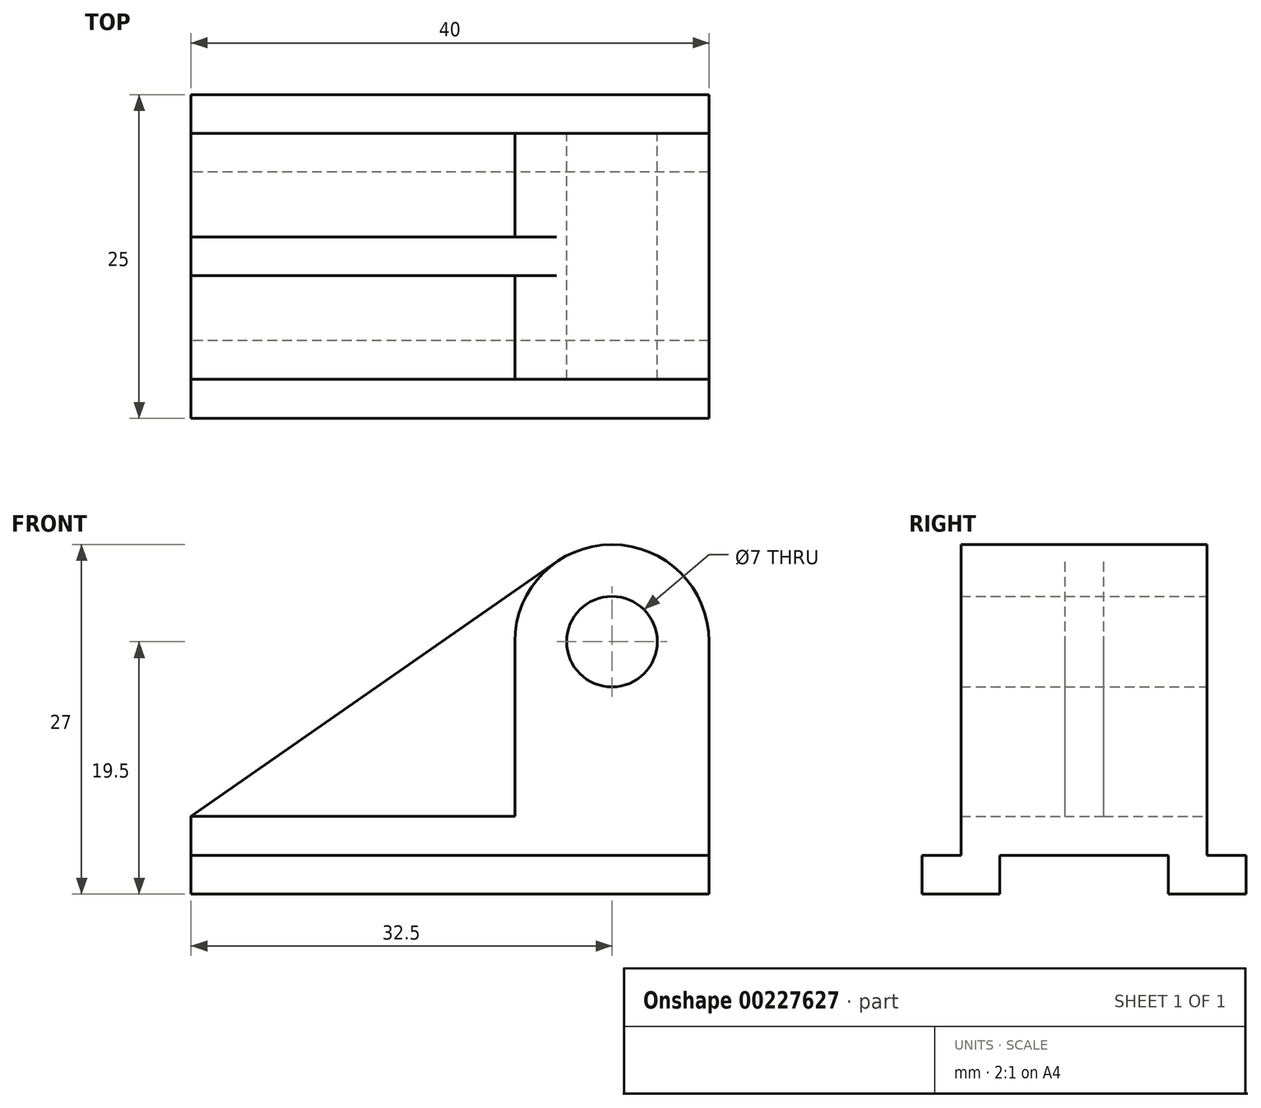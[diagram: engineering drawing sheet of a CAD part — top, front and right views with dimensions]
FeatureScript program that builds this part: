
annotation { "Feature Type Name" : "Feature", "Feature Type Description" : "" }
export const myFeature = defineFeature(function(context is Context, id is Id, definition is map)
    precondition{}
    {
        {
            var Q0;
            Q0=qCreatedBy(makeId("Right.planeOp"),FACE);
            var sketch = newSketch(context, id + "F0", { "sketchPlane" : qUnion([Q0])});
            skLineSegment(sketch, "E0", {"start": v(0, 0) * mm, "end": v(-6.5, 0) * mm});
            skLineSegment(sketch, "E1", {"start": v(-6.5, 0) * mm, "end": v(-6.5, -3) * mm});
            skLineSegment(sketch, "E2", {"start": v(-6.5, -3) * mm, "end": v(-12.5, -3) * mm});
            skLineSegment(sketch, "E3", {"start": v(-12.5, -3) * mm, "end": v(-12.5, 0) * mm});
            skLineSegment(sketch, "E4", {"start": v(-12.5, 0) * mm, "end": v(-9.5, 0) * mm});
            skLineSegment(sketch, "E5", {"start": v(-9.5, 0) * mm, "end": v(-9.5, 3) * mm});
            skLineSegment(sketch, "E6", {"start": v(-9.5, 3) * mm, "end": v(0, 3) * mm});
            skLineSegment(sketch, "E7", {"start": v(0, 3) * mm, "end": v(0, 0) * mm});
            skSolve(sketch);
        }
        {
            var Q0;
            Q0=makeQuery(id+"F0.imprint","IMPRINT",FACE,{"disambiguationData":[TD([[makeQuery(id+"F0.imprint","IMPRINT",EDGE,{"derivedFrom":sQuery(id+"F0.wireOp",EDGE,"E0")}),-1.0]])]});
            extrude(context, id + "F1", {"entities" : qUnion([Q0]), "depth" : 40 * mm});
        }
        {
            var Q0;
            Q0=makeQuery(id+"F1.opExtrude","SWEPT_BODY",BODY,{"disambiguationData":[OSD([sQuery(id+"F0.wireOp",EDGE,"E0"),sQuery(id+"F0.wireOp",EDGE,"E1"),sQuery(id+"F0.wireOp",EDGE,"E2"),sQuery(id+"F0.wireOp",EDGE,"E3"),sQuery(id+"F0.wireOp",EDGE,"E4"),sQuery(id+"F0.wireOp",EDGE,"E5"),sQuery(id+"F0.wireOp",EDGE,"E6"),sQuery(id+"F0.wireOp",EDGE,"E7")])]});
            var Q1;
            Q1=qCreatedBy(makeId("Front.planeOp"),FACE);
            mirror(context, id + "F2", {"operationType" : NewBodyOperationType.ADD, "entities" : qUnion([Q0]), "mirrorPlane" : qUnion([Q1])});
        }
        {
            var Q0;
            Q0=qCreatedBy(makeId("Front.planeOp"),FACE);
            var sketch = newSketch(context, id + "F3", { "sketchPlane" : qUnion([Q0])});
            skLineSegment(sketch, "E8.0", {"start": v(40, 3) * mm, "end": v(0, 3) * mm});
            skLineSegment(sketch, "E9", {"start": v(40, 3) * mm, "end": v(40, 16.5) * mm});
            skLineSegment(sketch, "E10", {"start": v(40, 16.5) * mm, "end": v(25, 16.5) * mm, "construction": true});
            skLineSegment(sketch, "E11", {"start": v(25, 16.5) * mm, "end": v(25, 3) * mm});
            skArc(sketch, "E12", {"start": v(40, 16.5) * mm, "mid": v(32.5, 24) * mm, "end": v(25, 16.5) * mm});
            skCircle(sketch, "E13", {"center": v(32.5, 16.5) * mm, "radius": 3.5 * mm});
            skLineSegment(sketch, "E14", {"start": v(28.62, 22.94) * mm, "end": v(0, 3) * mm});
            skSolve(sketch);
        }
        {
            var Q0;
            {var subQ1=sQuery(id+"F3.wireOp",EDGE,"E9");Q0=makeQuery(id+"F3.imprint","IMPRINT",FACE,{"disambiguationData":[TD([[makeQuery(id+"F3.imprint","IMPRINT",EDGE,{"derivedFrom":subQ1}),1.0]])]});}
            extrude(context, id + "F4", {"entities" : qUnion([Q0]), "operationType" : NewBodyOperationType.ADD, "endBound" : BoundingType.SYMMETRIC, "depth" : 19 * mm});
        }
        {
            var Q0;
            {var subQ3=sQuery(id+"F3.wireOp",EDGE,"E11");Q0=makeQuery(id+"F3.imprint","IMPRINT",FACE,{"disambiguationData":[TD([[makeQuery(id+"F3.imprint","IMPRINT",EDGE,{"derivedFrom":subQ3}),-1.0]])]});}
            extrude(context, id + "F5", {"entities" : qUnion([Q0]), "operationType" : NewBodyOperationType.ADD, "endBound" : BoundingType.SYMMETRIC, "depth" : 3 * mm});
        }
    });
